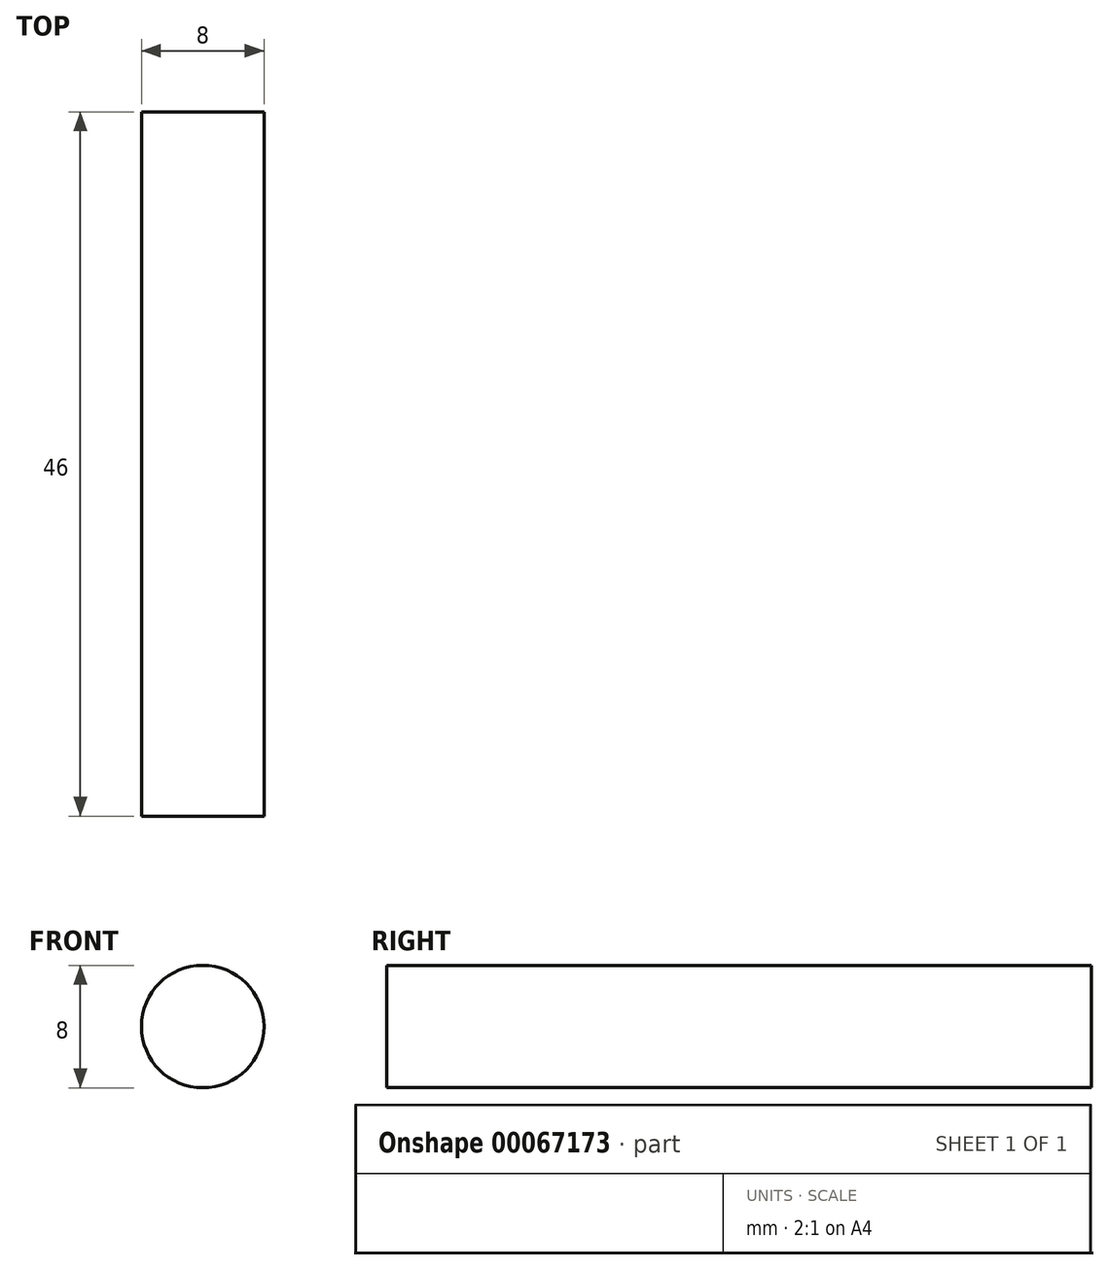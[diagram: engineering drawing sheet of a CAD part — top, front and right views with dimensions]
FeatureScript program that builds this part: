
annotation { "Feature Type Name" : "Feature", "Feature Type Description" : "" }
export const myFeature = defineFeature(function(context is Context, id is Id, definition is map)
    precondition{}
    {
        {
            var Q0;
            Q0=qCreatedBy(makeId("Front.planeOp"),FACE);
            var sketch = newSketch(context, id + "F0", { "sketchPlane" : qUnion([Q0])});
            skCircle(sketch, "E0", {"center": v(-12.64, 14.22) * mm, "radius": 4 * mm});
            skSolve(sketch);
        }
        {
            var Q0;
            Q0=makeQuery(id+"F0.imprint","IMPRINT",FACE,{"disambiguationData":[TD([[makeQuery(id+"F0.imprint","IMPRINT",EDGE,{"derivedFrom":sQuery(id+"F0.wireOp",EDGE,"E0")}),1.0]])]});
            extrude(context, id + "F1", {"entities" : qUnion([Q0]), "depth" : 46 * mm});
        }
    });
